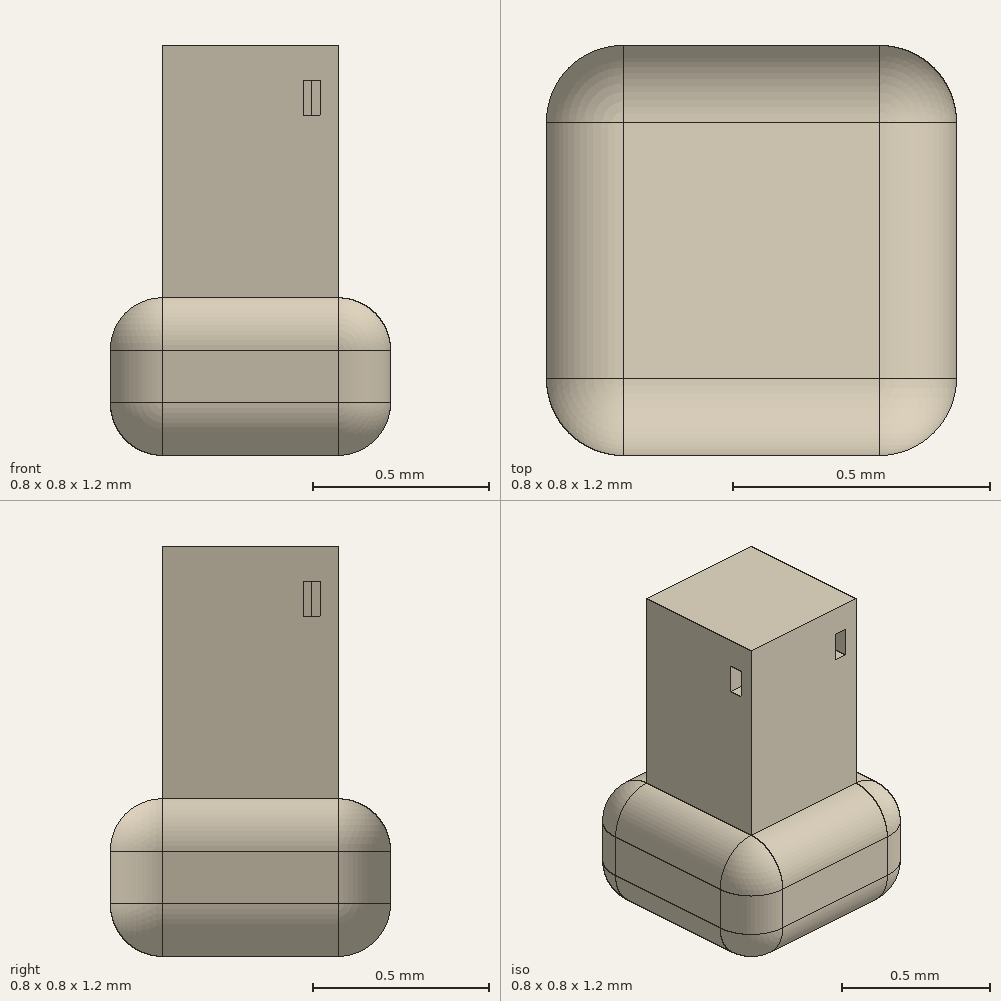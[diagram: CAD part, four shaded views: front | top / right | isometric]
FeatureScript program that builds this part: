
annotation { "Feature Type Name" : "Feature", "Feature Type Description" : "" }
export const myFeature = defineFeature(function(context is Context, id is Id, definition is map)
    precondition{}
    {
        {
            var Q0;
            Q0=qCreatedBy(makeId("Top.planeOp"),FACE);
            var sketch = newSketch(context, id + "F0", { "sketchPlane" : qUnion([Q0])});
            skLineSegment(sketch, "E0.bottom", {"start": v(-0.25, 0.25) * mm, "end": v(0.25, 0.25) * mm, "construction": true});
            skLineSegment(sketch, "E0.top", {"start": v(-0.25, -0.25) * mm, "end": v(0.25, -0.25) * mm, "construction": true});
            skLineSegment(sketch, "E0.left", {"start": v(-0.25, 0.25) * mm, "end": v(-0.25, -0.25) * mm, "construction": true});
            skLineSegment(sketch, "E0.right", {"start": v(0.25, 0.25) * mm, "end": v(0.25, -0.25) * mm, "construction": true});
            skLineSegment(sketch, "E1.0", {"start": v(-0.13, 0.2) * mm, "end": v(0.13, 0.2) * mm});
            skLineSegment(sketch, "E1.1", {"start": v(-0.2, 0.13) * mm, "end": v(-0.2, -0.13) * mm});
            skLineSegment(sketch, "E1.3", {"start": v(0.2, 0.13) * mm, "end": v(0.2, -0.13) * mm});
            skLineSegment(sketch, "E2.0", {"start": v(-0.17, 0.17) * mm, "end": v(0.18, 0.17) * mm, "construction": true});
            skLineSegment(sketch, "E2.1", {"start": v(-0.17, 0.17) * mm, "end": v(-0.17, -0.17) * mm, "construction": true});
            skLineSegment(sketch, "E2.2", {"start": v(-0.17, -0.17) * mm, "end": v(0.18, -0.17) * mm, "construction": true});
            skLineSegment(sketch, "E2.3", {"start": v(0.17, 0.17) * mm, "end": v(0.17, -0.18) * mm, "construction": true});
            skLineSegment(sketch, "E3.0", {"start": v(-0.13, 0.15) * mm, "end": v(0.13, 0.15) * mm});
            skLineSegment(sketch, "E3.1", {"start": v(-0.15, 0.13) * mm, "end": v(-0.15, -0.13) * mm});
            skLineSegment(sketch, "E3.3", {"start": v(0.15, 0.13) * mm, "end": v(0.15, -0.13) * mm});
            skArc(sketch, "E4", {"start": v(-0.2, -0.13) * mm, "mid": v(-0.17, -0.23) * mm, "end": v(-0.15, -0.13) * mm});
            skArc(sketch, "E5", {"start": v(-0.13, 0.2) * mm, "mid": v(-0.21, 0.21) * mm, "end": v(-0.2, 0.13) * mm});
            skArc(sketch, "E6", {"start": v(0.13, 0.15) * mm, "mid": v(0.14, 0.14) * mm, "end": v(0.15, 0.13) * mm});
            skArc(sketch, "E7", {"start": v(0.15, -0.13) * mm, "mid": v(0.18, -0.23) * mm, "end": v(0.2, -0.13) * mm});
            skArc(sketch, "E8.trimOffspring", {"start": v(-0.15, 0.13) * mm, "mid": v(-0.14, 0.14) * mm, "end": v(-0.13, 0.15) * mm});
            skArc(sketch, "E9.trimOffspring", {"start": v(0.2, 0.13) * mm, "mid": v(0.21, 0.21) * mm, "end": v(0.13, 0.2) * mm});
            skSolve(sketch);
        }
        {
            var Q0;
            Q0 = qSketchRegion(id + "F0", true);
            extrude(context, id + "F1", {"entities" : qUnion([Q0]), "depth" : .1 * mm, "offsetDistance" : 25 * mm});
        }
        {
            var Q0;
            Q0=qCreatedBy(makeId("Top.planeOp"),FACE);
            var sketch = newSketch(context, id + "F2", { "sketchPlane" : qUnion([Q0])});
            skLineSegment(sketch, "E10.bottom", {"start": v(-0.25, 0.25) * mm, "end": v(0.25, 0.25) * mm, "construction": true});
            skLineSegment(sketch, "E10.top", {"start": v(-0.25, -0.25) * mm, "end": v(0.25, -0.25) * mm, "construction": true});
            skLineSegment(sketch, "E10.left", {"start": v(-0.25, 0.25) * mm, "end": v(-0.25, -0.25) * mm, "construction": true});
            skLineSegment(sketch, "E10.right", {"start": v(0.25, 0.25) * mm, "end": v(0.25, -0.25) * mm, "construction": true});
            skLineSegment(sketch, "E11", {"start": v(-0.25, 0.25) * mm, "end": v(0.25, -0.25) * mm, "construction": true});
            skLineSegment(sketch, "E12.0", {"start": v(0.18, 0.18) * mm, "end": v(0.17, -0.25) * mm, "construction": true});
            skLineSegment(sketch, "E12.1", {"start": v(-0.25, 0.18) * mm, "end": v(0.18, 0.18) * mm, "construction": true});
            skLineSegment(sketch, "E13.0", {"start": v(-0.18, -0.18) * mm, "end": v(0.25, -0.18) * mm, "construction": true});
            skLineSegment(sketch, "E13.1", {"start": v(-0.17, 0.25) * mm, "end": v(-0.18, -0.18) * mm, "construction": true});
            skCircle(sketch, "E14", {"center": v(-0.18, -0.18) * mm, "radius": 0.05 * mm});
            skCircle(sketch, "E15", {"center": v(-0.18, 0.18) * mm, "radius": 0.05 * mm});
            skCircle(sketch, "E16", {"center": v(0.18, 0.18) * mm, "radius": 0.05 * mm});
            skCircle(sketch, "E17", {"center": v(0.17, -0.18) * mm, "radius": 0.05 * mm});
            skLineSegment(sketch, "E18.0", {"start": v(0.15, 0.15) * mm, "end": v(0.15, -0.25) * mm, "construction": true});
            skLineSegment(sketch, "E18.1", {"start": v(-0.25, 0.15) * mm, "end": v(0.15, 0.15) * mm, "construction": true});
            skLineSegment(sketch, "E19.0", {"start": v(0.2, 0.2) * mm, "end": v(0.2, -0.25) * mm, "construction": true});
            skLineSegment(sketch, "E19.1", {"start": v(-0.25, 0.2) * mm, "end": v(0.2, 0.2) * mm, "construction": true});
            skLineSegment(sketch, "E20.0", {"start": v(-0.15, -0.15) * mm, "end": v(0.25, -0.15) * mm, "construction": true});
            skLineSegment(sketch, "E20.1", {"start": v(-0.15, 0.25) * mm, "end": v(-0.15, -0.15) * mm, "construction": true});
            skLineSegment(sketch, "E21.0", {"start": v(-0.2, -0.2) * mm, "end": v(0.25, -0.2) * mm, "construction": true});
            skLineSegment(sketch, "E21.1", {"start": v(-0.2, 0.25) * mm, "end": v(-0.2, -0.2) * mm, "construction": true});
            skLineSegment(sketch, "E22", {"start": v(0.18, -0.15) * mm, "end": v(-0.15, 0.18) * mm});
            skLineSegment(sketch, "E23", {"start": v(0.15, -0.18) * mm, "end": v(-0.18, 0.15) * mm});
            skLineSegment(sketch, "E24.bottom", {"start": v(-0.15, -0.15) * mm, "end": v(-0.2, -0.15) * mm, "construction": true});
            skLineSegment(sketch, "E24.top", {"start": v(-0.15, -0.2) * mm, "end": v(-0.2, -0.2) * mm});
            skLineSegment(sketch, "E24.left", {"start": v(-0.15, -0.15) * mm, "end": v(-0.15, -0.2) * mm, "construction": true});
            skLineSegment(sketch, "E24.right", {"start": v(-0.2, -0.15) * mm, "end": v(-0.2, -0.2) * mm});
            skLineSegment(sketch, "E25.bottom", {"start": v(0.15, 0.15) * mm, "end": v(0.2, 0.15) * mm, "construction": true});
            skLineSegment(sketch, "E25.top", {"start": v(0.15, 0.2) * mm, "end": v(0.2, 0.2) * mm});
            skLineSegment(sketch, "E25.left", {"start": v(0.15, 0.15) * mm, "end": v(0.15, 0.2) * mm, "construction": true});
            skLineSegment(sketch, "E25.right", {"start": v(0.2, 0.15) * mm, "end": v(0.2, 0.2) * mm});
            skLineSegment(sketch, "E26", {"start": v(-0.17, -0.15) * mm, "end": v(0.15, 0.18) * mm});
            skLineSegment(sketch, "E27", {"start": v(0.17, 0.15) * mm, "end": v(-0.15, -0.17) * mm});
            skLineSegment(sketch, "E28", {"start": v(0.2, 0.2) * mm, "end": v(0.25, 0.2) * mm});
            skLineSegment(sketch, "E29", {"start": v(0.2, 0.15) * mm, "end": v(0.25, 0.15) * mm});
            skLineSegment(sketch, "E30", {"start": v(0.25, 0.15) * mm, "end": v(0.25, 0.2) * mm});
            skLineSegment(sketch, "E31", {"start": v(0.15, -0.2) * mm, "end": v(0.15, -0.25) * mm});
            skLineSegment(sketch, "E32", {"start": v(0.15, -0.25) * mm, "end": v(0.2, -0.25) * mm});
            skLineSegment(sketch, "E33", {"start": v(0.2, -0.2) * mm, "end": v(0.2, -0.25) * mm});
            skLineSegment(sketch, "E34", {"start": v(-0.2, -0.15) * mm, "end": v(-0.25, -0.15) * mm});
            skLineSegment(sketch, "E35", {"start": v(-0.2, -0.2) * mm, "end": v(-0.25, -0.2) * mm});
            skLineSegment(sketch, "E36", {"start": v(-0.25, -0.2) * mm, "end": v(-0.25, -0.15) * mm});
            skLineSegment(sketch, "E37", {"start": v(-0.15, 0.2) * mm, "end": v(-0.15, 0.25) * mm});
            skLineSegment(sketch, "E38", {"start": v(-0.2, 0.2) * mm, "end": v(-0.2, 0.25) * mm});
            skLineSegment(sketch, "E39", {"start": v(-0.2, 0.25) * mm, "end": v(-0.15, 0.25) * mm});
            skSolve(sketch);
        }
        {
            var Q0;
            Q0 = qSketchRegion(id + "F2", true);
            extrude(context, id + "F3", {"entities" : qUnion([Q0]), "depth" : .1 * mm, "offsetDistance" : 25 * mm});
        }
        {
            var Q0;
            Q0=qCreatedBy(makeId("Top.planeOp"),FACE);
            var sketch = newSketch(context, id + "F4", { "sketchPlane" : qUnion([Q0])});
            skCircle(sketch, "E40", {"center": v(0, 0) * mm, "radius": 0.05 * mm});
            skSolve(sketch);
        }
        {
            var Q0;
            Q0 = qSketchRegion(id + "F4", true);
            extrude(context, id + "F5", {"entities" : qUnion([Q0]), "depth" : .1 * mm, "offsetDistance" : 25 * mm});
        }
        {
            var Q0;
            Q0=qCreatedBy(makeId("Top.planeOp"),FACE);
            var sketch = newSketch(context, id + "F6", { "sketchPlane" : qUnion([Q0])});
            skLineSegment(sketch, "E41.bottom", {"start": v(-0.25, 0.25) * mm, "end": v(0.25, 0.25) * mm});
            skLineSegment(sketch, "E41.top", {"start": v(-0.25, -0.25) * mm, "end": v(0.25, -0.25) * mm});
            skLineSegment(sketch, "E41.left", {"start": v(-0.25, 0.25) * mm, "end": v(-0.25, -0.25) * mm});
            skLineSegment(sketch, "E41.right", {"start": v(0.25, 0.25) * mm, "end": v(0.25, -0.25) * mm});
            skLineSegment(sketch, "E42", {"start": v(-0.25, 0.25) * mm, "end": v(0.25, -0.25) * mm, "construction": true});
            skSolve(sketch);
        }
        {
            var Q0;
            Q0 = qSketchRegion(id + "F6", true);
            extrude(context, id + "F7", {"entities" : qUnion([Q0]), "depth" : .1 * mm, "offsetDistance" : 25 * mm});
        }
        {
            var Q0;
            Q0=makeQuery(id+"F7.opExtrude","CAP_FACE",FACE,{"disambiguationData":[OSD([sQuery(id+"F6.wireOp",EDGE,"E41.bottom"),sQuery(id+"F6.wireOp",EDGE,"E41.top"),sQuery(id+"F6.wireOp",EDGE,"E41.left"),sQuery(id+"F6.wireOp",EDGE,"E41.right")])],"isStart":false});
            var sketch = newSketch(context, id + "F8", { "sketchPlane" : qUnion([Q0])});
            skLineSegment(sketch, "E43.bottom", {"start": v(-0.25, 0.25) * mm, "end": v(-0.2, 0.25) * mm});
            skLineSegment(sketch, "E43.left", {"start": v(-0.25, 0.25) * mm, "end": v(-0.25, -0.15) * mm});
            skLineSegment(sketch, "E43.right", {"start": v(0.25, 0.25) * mm, "end": v(0.25, 0.2) * mm});
            skLineSegment(sketch, "E44.bottom", {"start": v(0.25, 0.25) * mm, "end": v(-0.15, 0.25) * mm});
            skLineSegment(sketch, "E44.top", {"start": v(0.25, 0.2) * mm, "end": v(-0.15, 0.2) * mm});
            skLineSegment(sketch, "E44.right", {"start": v(-0.15, 0.25) * mm, "end": v(-0.15, 0.2) * mm});
            skLineSegment(sketch, "E45.top", {"start": v(-0.25, -0.15) * mm, "end": v(-0.2, -0.15) * mm});
            skLineSegment(sketch, "E45.right", {"start": v(-0.2, 0.25) * mm, "end": v(-0.2, -0.15) * mm});
            skLineSegment(sketch, "E46.bottom", {"start": v(-0.25, -0.25) * mm, "end": v(0.15, -0.25) * mm});
            skLineSegment(sketch, "E46.top", {"start": v(-0.25, -0.2) * mm, "end": v(0.15, -0.2) * mm});
            skLineSegment(sketch, "E46.left", {"start": v(-0.25, -0.25) * mm, "end": v(-0.25, -0.2) * mm});
            skLineSegment(sketch, "E46.right", {"start": v(0.15, -0.25) * mm, "end": v(0.15, -0.2) * mm});
            skLineSegment(sketch, "E47.bottom", {"start": v(0.25, -0.25) * mm, "end": v(0.2, -0.25) * mm});
            skLineSegment(sketch, "E47.top", {"start": v(0.25, 0.15) * mm, "end": v(0.2, 0.15) * mm});
            skLineSegment(sketch, "E47.left", {"start": v(0.25, -0.25) * mm, "end": v(0.25, 0.15) * mm});
            skLineSegment(sketch, "E47.right", {"start": v(0.2, -0.25) * mm, "end": v(0.2, 0.15) * mm});
            skLineSegment(sketch, "E48.bottom", {"start": v(-0.17, 0.17) * mm, "end": v(0.17, 0.17) * mm});
            skLineSegment(sketch, "E48.top", {"start": v(-0.17, -0.18) * mm, "end": v(0.18, -0.17) * mm});
            skLineSegment(sketch, "E48.left", {"start": v(-0.17, 0.17) * mm, "end": v(-0.17, -0.18) * mm});
            skLineSegment(sketch, "E48.right", {"start": v(0.17, 0.17) * mm, "end": v(0.18, -0.18) * mm});
            skLineSegment(sketch, "E49.trimOffspring", {"start": v(-0.15, 0.25) * mm, "end": v(0.25, 0.25) * mm});
            skLineSegment(sketch, "E50.trimOffspring", {"start": v(0.25, 0.15) * mm, "end": v(0.25, -0.25) * mm});
            skLineSegment(sketch, "E51.trimOffspring", {"start": v(0.2, -0.25) * mm, "end": v(0.25, -0.25) * mm});
            skLineSegment(sketch, "E52.trimOffspring", {"start": v(-0.25, -0.2) * mm, "end": v(-0.25, -0.25) * mm});
            skSolve(sketch);
        }
        {
            var Q0;
            Q0 = qSketchRegion(id + "F8", true);
            extrude(context, id + "F9", {"entities" : qUnion([Q0]), "operationType" : NewBodyOperationType.ADD, "depth" : .1 * mm, "offsetDistance" : 25 * mm});
        }
        {
            var Q0;
            Q0=makeQuery(id+"F9.opExtrude","CAP_FACE",FACE,{"disambiguationData":[OSD([sQuery(id+"F8.wireOp",EDGE,"E48.bottom"),sQuery(id+"F8.wireOp",EDGE,"E48.top"),sQuery(id+"F8.wireOp",EDGE,"E48.left"),sQuery(id+"F8.wireOp",EDGE,"E48.right")])],"isStart":false});
            var sketch = newSketch(context, id + "F10", { "sketchPlane" : qUnion([Q0])});
            skLineSegment(sketch, "E53.bottom", {"start": v(-0.25, 0.25) * mm, "end": v(0.25, 0.25) * mm});
            skLineSegment(sketch, "E53.top", {"start": v(-0.25, -0.25) * mm, "end": v(0.25, -0.25) * mm});
            skLineSegment(sketch, "E53.left", {"start": v(-0.25, 0.25) * mm, "end": v(-0.25, -0.25) * mm});
            skLineSegment(sketch, "E53.right", {"start": v(0.25, 0.25) * mm, "end": v(0.25, -0.25) * mm});
            skLineSegment(sketch, "E54", {"start": v(-0.25, 0.25) * mm, "end": v(0.25, -0.25) * mm, "construction": true});
            skSolve(sketch);
        }
        {
            var Q0;
            Q0 = qSketchRegion(id + "F10", true);
            extrude(context, id + "F11", {"entities" : qUnion([Q0]), "operationType" : NewBodyOperationType.ADD, "depth" : .77 * mm, "offsetDistance" : 25 * mm});
        }
        {
            var Q0;
            Q0=makeQuery(id+"F11.opExtrude","CAP_FACE",FACE,{"disambiguationData":[OSD([sQuery(id+"F10.wireOp",EDGE,"E53.bottom"),sQuery(id+"F10.wireOp",EDGE,"E53.top"),sQuery(id+"F10.wireOp",EDGE,"E53.left"),sQuery(id+"F10.wireOp",EDGE,"E53.right")])],"isStart":false});
            var sketch = newSketch(context, id + "F12", { "sketchPlane" : qUnion([Q0])});
            skLineSegment(sketch, "E55.bottom", {"start": v(0.25, 0.25) * mm, "end": v(-0.15, 0.25) * mm});
            skLineSegment(sketch, "E55.top", {"start": v(0.25, 0.2) * mm, "end": v(-0.15, 0.2) * mm});
            skLineSegment(sketch, "E55.left", {"start": v(0.25, 0.25) * mm, "end": v(0.25, 0.2) * mm});
            skLineSegment(sketch, "E55.right", {"start": v(-0.15, 0.25) * mm, "end": v(-0.15, 0.2) * mm});
            skLineSegment(sketch, "E56.bottom", {"start": v(-0.25, 0.25) * mm, "end": v(-0.2, 0.25) * mm});
            skLineSegment(sketch, "E56.top", {"start": v(-0.25, -0.15) * mm, "end": v(-0.2, -0.15) * mm});
            skLineSegment(sketch, "E56.left", {"start": v(-0.25, 0.25) * mm, "end": v(-0.25, -0.15) * mm});
            skLineSegment(sketch, "E56.right", {"start": v(-0.2, 0.25) * mm, "end": v(-0.2, -0.15) * mm});
            skLineSegment(sketch, "E57.bottom", {"start": v(-0.25, -0.25) * mm, "end": v(0.15, -0.25) * mm});
            skLineSegment(sketch, "E57.top", {"start": v(-0.25, -0.2) * mm, "end": v(0.15, -0.2) * mm});
            skLineSegment(sketch, "E57.left", {"start": v(-0.25, -0.25) * mm, "end": v(-0.25, -0.2) * mm});
            skLineSegment(sketch, "E57.right", {"start": v(0.15, -0.25) * mm, "end": v(0.15, -0.2) * mm});
            skLineSegment(sketch, "E58.bottom", {"start": v(0.25, -0.25) * mm, "end": v(0.2, -0.25) * mm});
            skLineSegment(sketch, "E58.top", {"start": v(0.25, 0.15) * mm, "end": v(0.2, 0.15) * mm});
            skLineSegment(sketch, "E58.left", {"start": v(0.25, -0.25) * mm, "end": v(0.25, 0.15) * mm});
            skLineSegment(sketch, "E58.right", {"start": v(0.2, -0.25) * mm, "end": v(0.2, 0.15) * mm});
            skLineSegment(sketch, "E59.bottom", {"start": v(-0.17, 0.17) * mm, "end": v(0.18, 0.17) * mm});
            skLineSegment(sketch, "E59.top", {"start": v(-0.17, -0.18) * mm, "end": v(0.18, -0.17) * mm});
            skLineSegment(sketch, "E59.left", {"start": v(-0.17, 0.17) * mm, "end": v(-0.17, -0.18) * mm});
            skLineSegment(sketch, "E59.right", {"start": v(0.18, 0.17) * mm, "end": v(0.18, -0.17) * mm});
            skSolve(sketch);
        }
        {
            var Q0;
            Q0 = qSketchRegion(id + "F12", true);
            extrude(context, id + "F13", {"entities" : qUnion([Q0]), "operationType" : NewBodyOperationType.ADD, "depth" : .1 * mm, "offsetDistance" : 25 * mm});
        }
        {
            var Q0;
            Q0=makeQuery(id+"F13.opExtrude","CAP_FACE",FACE,{"disambiguationData":[OSD([sQuery(id+"F12.wireOp",EDGE,"E59.bottom"),sQuery(id+"F12.wireOp",EDGE,"E59.top"),sQuery(id+"F12.wireOp",EDGE,"E59.left"),sQuery(id+"F12.wireOp",EDGE,"E59.right")])],"isStart":false});
            var sketch = newSketch(context, id + "F14", { "sketchPlane" : qUnion([Q0])});
            skLineSegment(sketch, "E60.bottom", {"start": v(-0.25, 0.25) * mm, "end": v(0.25, 0.25) * mm});
            skLineSegment(sketch, "E60.top", {"start": v(-0.25, -0.25) * mm, "end": v(0.25, -0.25) * mm});
            skLineSegment(sketch, "E60.left", {"start": v(-0.25, 0.25) * mm, "end": v(-0.25, -0.25) * mm});
            skLineSegment(sketch, "E60.right", {"start": v(0.25, 0.25) * mm, "end": v(0.25, -0.25) * mm});
            skLineSegment(sketch, "E61", {"start": v(-0.25, 0.25) * mm, "end": v(0.25, -0.25) * mm, "construction": true});
            skSolve(sketch);
        }
        {
            var Q0;
            Q0 = qSketchRegion(id + "F14", true);
            extrude(context, id + "F15", {"entities" : qUnion([Q0]), "operationType" : NewBodyOperationType.ADD, "depth" : .1 * mm, "offsetDistance" : 25 * mm});
        }
        {
            var Q0;
            Q0=qCreatedBy(makeId("Top.planeOp"),FACE);
            var sketch = newSketch(context, id + "F16", { "sketchPlane" : qUnion([Q0])});
            skPoint(sketch, "E62.middle", {"position": v(0, 0) * mm});
            skLineSegment(sketch, "E63.0", {"start": v(0.25, 0.25) * mm, "end": v(-0.25, 0.25) * mm});
            skLineSegment(sketch, "E63.1", {"start": v(0.25, -0.25) * mm, "end": v(0.25, 0.25) * mm});
            skLineSegment(sketch, "E63.2", {"start": v(0.25, -0.25) * mm, "end": v(-0.25, -0.25) * mm});
            skLineSegment(sketch, "E63.3", {"start": v(-0.25, -0.25) * mm, "end": v(-0.25, 0.25) * mm});
            skSolve(sketch);
        }
        {
            var Q0;
            Q0 = qSketchRegion(id + "F16", true);
            extrude(context, id + "F17", {"entities" : qUnion([Q0]), "depth" : .3 * mm, "offsetDistance" : 25 * mm});
        }
        {
            var Q0;
            Q0=makeQuery(id+"F17.opExtrude","CAP_FACE",FACE,{"disambiguationData":[OSD([sQuery(id+"F16.wireOp",EDGE,"E63.0"),sQuery(id+"F16.wireOp",EDGE,"E63.1"),sQuery(id+"F16.wireOp",EDGE,"E63.2"),sQuery(id+"F16.wireOp",EDGE,"E63.3")])],"isStart":true});
            shell(context, id + "F18", {"entities" : qUnion([Q0]), "thickness" : .15 * mm, "oppositeDirection" : true});
        }
        {
            var Q0;
            Q0=makeQuery(id+"F17.opExtrude","SWEPT_FACE",FACE,{"disambiguationData":[OSD([sQuery(id+"F16.wireOp",EDGE,"E63.2")])]});
            var Q1;
            Q1=makeQuery(id+"F17.opExtrude","SWEPT_FACE",FACE,{"disambiguationData":[OSD([sQuery(id+"F16.wireOp",EDGE,"E63.3")])]});
            var Q2;
            Q2=makeQuery(id+"F17.opExtrude","CAP_FACE",FACE,{"disambiguationData":[OSD([sQuery(id+"F16.wireOp",EDGE,"E63.0"),sQuery(id+"F16.wireOp",EDGE,"E63.1"),sQuery(id+"F16.wireOp",EDGE,"E63.2"),sQuery(id+"F16.wireOp",EDGE,"E63.3")])],"isStart":false});
            var Q3;
            Q3=makeQuery(id+"F17.opExtrude","SWEPT_FACE",FACE,{"disambiguationData":[OSD([sQuery(id+"F16.wireOp",EDGE,"E63.1")])]});
            var Q4;
            Q4=makeQuery(id+"F17.opExtrude","SWEPT_FACE",FACE,{"disambiguationData":[OSD([sQuery(id+"F16.wireOp",EDGE,"E63.0")])]});
            fillet(context, id + "F19", {"entities" : qUnion([Q0, Q1, Q2, Q3, Q4]), "tangentPropagation" : true, "radius" : .15 * mm, "defaultsChanged" : true, "vertexSettings" : [], "allowEdgeOverflow" : false});
        }
    });
